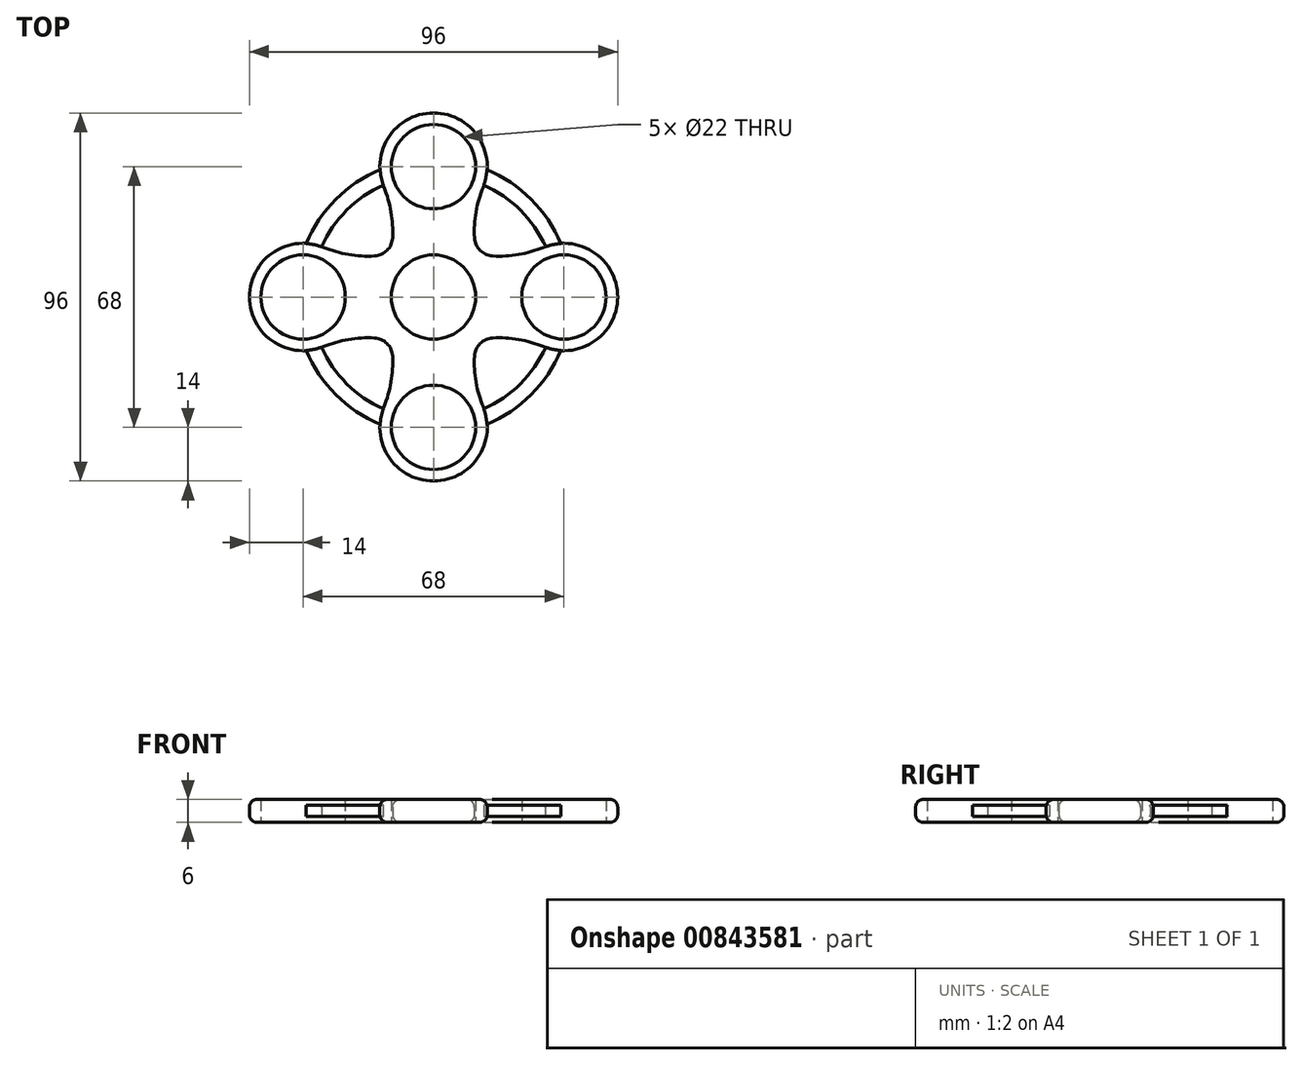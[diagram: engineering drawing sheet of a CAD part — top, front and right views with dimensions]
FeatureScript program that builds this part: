
annotation { "Feature Type Name" : "Feature", "Feature Type Description" : "" }
export const myFeature = defineFeature(function(context is Context, id is Id, definition is map)
    precondition{}
    {
        {
            var Q0;
            Q0=qCreatedBy(makeId("Top.planeOp"),FACE);
            var sketch = newSketch(context, id + "F0", { "sketchPlane" : qUnion([Q0])});
            skCircle(sketch, "E0", {"center": v(0, 0) * mm, "radius": 11 * mm});
            skLineSegment(sketch, "E1", {"start": v(0, 0) * mm, "end": v(0, 14) * mm});
            skCircle(sketch, "E2", {"center": v(0, 34) * mm, "radius": 11 * mm});
            skArc(sketch, "E3", {"start": v(12.94, 28.66) * mm, "mid": v(0, 48) * mm, "end": v(-12.94, 28.66) * mm});
            skArc(sketch, "E4", {"start": v(12.94, 28.66) * mm, "mid": v(11.07, 22.16) * mm, "end": v(10.68, 15.4) * mm});
            skArc(sketch, "E5.MirrorCS", {"start": v(-12.94, 28.66) * mm, "mid": v(-11.07, 22.16) * mm, "end": v(-10.68, 15.4) * mm});
            skArc(sketch, "E6.1.0", {"start": v(-28.66, 12.94) * mm, "mid": v(-22.16, 11.07) * mm, "end": v(-15.4, 10.68) * mm});
            skArc(sketch, "E6.1.1", {"start": v(-28.66, 12.94) * mm, "mid": v(-48, 0) * mm, "end": v(-28.66, -12.94) * mm});
            skCircle(sketch, "E6.1.2", {"center": v(-34, 0) * mm, "radius": 11 * mm});
            skArc(sketch, "E6.1.3", {"start": v(-28.66, -12.94) * mm, "mid": v(-22.16, -11.07) * mm, "end": v(-15.4, -10.68) * mm});
            skArc(sketch, "E6.2.0", {"start": v(-12.94, -28.66) * mm, "mid": v(-11.07, -22.16) * mm, "end": v(-10.68, -15.4) * mm});
            skArc(sketch, "E6.2.1", {"start": v(-12.94, -28.66) * mm, "mid": v(0, -48) * mm, "end": v(12.94, -28.66) * mm});
            skCircle(sketch, "E6.2.2", {"center": v(0, -34) * mm, "radius": 11 * mm});
            skArc(sketch, "E6.2.3", {"start": v(12.94, -28.66) * mm, "mid": v(11.07, -22.16) * mm, "end": v(10.68, -15.4) * mm});
            skArc(sketch, "E6.3.0", {"start": v(28.66, -12.94) * mm, "mid": v(22.16, -11.07) * mm, "end": v(15.4, -10.68) * mm});
            skArc(sketch, "E6.3.1", {"start": v(28.66, -12.94) * mm, "mid": v(48, 0) * mm, "end": v(28.66, 12.94) * mm});
            skCircle(sketch, "E6.3.2", {"center": v(34, 0) * mm, "radius": 11 * mm});
            skArc(sketch, "E6.3.3", {"start": v(28.66, 12.94) * mm, "mid": v(22.16, 11.07) * mm, "end": v(15.4, 10.68) * mm});
            skPoint(sketch, "E7.visualSharp", {"position": v(-11.2, 11.2) * mm});
            skArc(sketch, "E7.filletArc", {"start": v(-15.4, 10.68) * mm, "mid": v(-12.13, 12.13) * mm, "end": v(-10.68, 15.4) * mm});
            skPoint(sketch, "E8.visualSharp", {"position": v(11.2, 11.2) * mm});
            skArc(sketch, "E8.filletArc", {"start": v(10.68, 15.4) * mm, "mid": v(12.13, 12.13) * mm, "end": v(15.4, 10.68) * mm});
            skPoint(sketch, "E9.visualSharp", {"position": v(-11.2, -11.2) * mm});
            skArc(sketch, "E9.filletArc", {"start": v(-10.68, -15.4) * mm, "mid": v(-12.13, -12.13) * mm, "end": v(-15.4, -10.68) * mm});
            skPoint(sketch, "E10.visualSharp", {"position": v(11.2, -11.2) * mm});
            skArc(sketch, "E10.filletArc", {"start": v(15.4, -10.68) * mm, "mid": v(12.13, -12.13) * mm, "end": v(10.68, -15.4) * mm});
            skSolve(sketch);
        }
        {
            var Q0;
            Q0 = qSketchRegion(id + "F0", true);
            extrude(context, id + "F1", {"entities" : qUnion([Q0]), "oppositeDirection" : true, "depth" : 1.5 * mm, "offsetDistance" : 25 * mm});
        }
        {
            var Q0;
            Q0=qCreatedBy(makeId("Top.planeOp"),FACE);
            var sketch = newSketch(context, id + "F2", { "sketchPlane" : qUnion([Q0])});
            skCircle(sketch, "E11", {"center": v(0, 0) * mm, "radius": 11 * mm});
            skCircle(sketch, "E12", {"center": v(0, 34) * mm, "radius": 11 * mm});
            skCircle(sketch, "E13.1.0", {"center": v(-34, 0) * mm, "radius": 11 * mm});
            skCircle(sketch, "E13.2.0", {"center": v(0, -34) * mm, "radius": 11 * mm});
            skCircle(sketch, "E13.3.0", {"center": v(34, 0) * mm, "radius": 11 * mm});
            skArc(sketch, "E14", {"start": v(12.94, 28.66) * mm, "mid": v(13.05, 28.92) * mm, "end": v(13.14, 29.18) * mm});
            skPoint(sketch, "E15.start.orphan", {"position": v(0, 17) * mm});
            skArc(sketch, "E16", {"start": v(12.94, 28.66) * mm, "mid": v(11.07, 22.16) * mm, "end": v(10.68, 15.4) * mm});
            skArc(sketch, "E17.MirrorC", {"start": v(-12.94, 28.66) * mm, "mid": v(-11.07, 22.16) * mm, "end": v(-10.68, 15.4) * mm});
            skArc(sketch, "E18.1.0", {"start": v(-28.66, 12.94) * mm, "mid": v(-22.16, 11.07) * mm, "end": v(-15.4, 10.68) * mm});
            skArc(sketch, "E18.1.1", {"start": v(-28.66, -12.94) * mm, "mid": v(-22.16, -11.07) * mm, "end": v(-15.4, -10.68) * mm});
            skArc(sketch, "E18.2.1", {"start": v(12.94, -28.66) * mm, "mid": v(11.07, -22.16) * mm, "end": v(10.68, -15.4) * mm});
            skArc(sketch, "E18.3.0", {"start": v(28.66, -12.94) * mm, "mid": v(22.16, -11.07) * mm, "end": v(15.4, -10.68) * mm});
            skArc(sketch, "E18.3.1", {"start": v(28.66, 12.94) * mm, "mid": v(22.16, 11.07) * mm, "end": v(15.4, 10.68) * mm});
            skArc(sketch, "E19", {"start": v(-28.66, 12.94) * mm, "mid": v(-28.92, 13.05) * mm, "end": v(-29.18, 13.14) * mm});
            skArc(sketch, "E20", {"start": v(-12.94, -28.66) * mm, "mid": v(-13.05, -28.92) * mm, "end": v(-13.14, -29.18) * mm});
            skArc(sketch, "E21", {"start": v(28.66, -12.94) * mm, "mid": v(28.92, -13.05) * mm, "end": v(29.18, -13.14) * mm});
            skArc(sketch, "E22.trimOffspring", {"start": v(-12.94, -28.66) * mm, "mid": v(-11.07, -22.16) * mm, "end": v(-10.68, -15.4) * mm});
            skPoint(sketch, "E23.visualSharp", {"position": v(-11.2, 11.2) * mm});
            skArc(sketch, "E23.filletArc", {"start": v(-15.4, 10.68) * mm, "mid": v(-12.13, 12.13) * mm, "end": v(-10.68, 15.4) * mm});
            skPoint(sketch, "E24.visualSharp", {"position": v(-11.2, -11.2) * mm});
            skArc(sketch, "E24.filletArc", {"start": v(-10.68, -15.4) * mm, "mid": v(-12.13, -12.13) * mm, "end": v(-15.4, -10.68) * mm});
            skPoint(sketch, "E25.visualSharp", {"position": v(11.2, 11.2) * mm});
            skArc(sketch, "E25.filletArc", {"start": v(10.68, 15.4) * mm, "mid": v(12.13, 12.13) * mm, "end": v(15.4, 10.68) * mm});
            skPoint(sketch, "E26.visualSharp", {"position": v(11.2, -11.2) * mm});
            skArc(sketch, "E26.filletArc", {"start": v(15.4, -10.68) * mm, "mid": v(12.13, -12.13) * mm, "end": v(10.68, -15.4) * mm});
            skArc(sketch, "E27", {"start": v(-13.98, 33.18) * mm, "mid": v(-25.46, 25.46) * mm, "end": v(-33.18, 13.98) * mm});
            skArc(sketch, "E28", {"start": v(-13.14, 29.18) * mm, "mid": v(-22.63, 22.63) * mm, "end": v(-29.18, 13.14) * mm});
            skArc(sketch, "E29.trimOffspring", {"start": v(-13.14, 29.18) * mm, "mid": v(-13.05, 28.92) * mm, "end": v(-12.94, 28.66) * mm});
            skArc(sketch, "E30.trimOffspring", {"start": v(-33.18, 13.98) * mm, "mid": v(-48, 0) * mm, "end": v(-33.18, -13.98) * mm});
            skArc(sketch, "E31.trimOffspring", {"start": v(-29.18, -13.14) * mm, "mid": v(-22.63, -22.63) * mm, "end": v(-13.14, -29.18) * mm});
            skArc(sketch, "E32.trimOffspring", {"start": v(-33.18, -13.98) * mm, "mid": v(-25.46, -25.46) * mm, "end": v(-13.98, -33.18) * mm});
            skArc(sketch, "E33.trimOffspring", {"start": v(-29.18, -13.14) * mm, "mid": v(-28.92, -13.05) * mm, "end": v(-28.66, -12.94) * mm});
            skArc(sketch, "E34.trimOffspring", {"start": v(-13.98, -33.18) * mm, "mid": v(0, -48) * mm, "end": v(13.98, -33.18) * mm});
            skArc(sketch, "E35.trimOffspring", {"start": v(13.14, -29.18) * mm, "mid": v(22.63, -22.63) * mm, "end": v(29.18, -13.14) * mm});
            skArc(sketch, "E36.trimOffspring", {"start": v(13.98, -33.18) * mm, "mid": v(25.46, -25.46) * mm, "end": v(33.18, -13.98) * mm});
            skArc(sketch, "E37.trimOffspring", {"start": v(13.14, -29.18) * mm, "mid": v(13.05, -28.92) * mm, "end": v(12.94, -28.66) * mm});
            skArc(sketch, "E38.trimOffspring", {"start": v(29.18, 13.14) * mm, "mid": v(22.63, 22.63) * mm, "end": v(13.14, 29.18) * mm});
            skArc(sketch, "E39.trimOffspring", {"start": v(33.18, 13.98) * mm, "mid": v(25.46, 25.46) * mm, "end": v(13.98, 33.18) * mm});
            skArc(sketch, "E40.trimOffspring", {"start": v(33.18, -13.98) * mm, "mid": v(48, 0) * mm, "end": v(33.18, 13.98) * mm});
            skArc(sketch, "E41.trimOffspring", {"start": v(29.18, 13.14) * mm, "mid": v(28.92, 13.05) * mm, "end": v(28.66, 12.94) * mm});
            skArc(sketch, "E42.trimOffspring", {"start": v(13.98, 33.18) * mm, "mid": v(0, 48) * mm, "end": v(-13.98, 33.18) * mm});
            skSolve(sketch);
        }
        {
            var Q0;
            Q0 = qSketchRegion(id + "F2", true);
            extrude(context, id + "F3", {"entities" : qUnion([Q0]), "depth" : 3 * mm, "offsetDistance" : 25 * mm});
        }
        {
            var Q0;
            Q0=qCreatedBy(makeId("Top.planeOp"),FACE);
            cPlane(context, id + "F4", {"entities" : qUnion([Q0]), "cplaneType" : CPlaneType.OFFSET, "offset" : 1.5 * mm, "width" : 150 * mm, "height" : 150 * mm});
        }
        {
            var Q0;
            Q0=makeQuery(id+"F1.opExtrude","SWEPT_BODY",BODY,{"disambiguationData":[OSD([sQuery(id+"F0.wireOp",EDGE,"E0"),sQuery(id+"F0.wireOp",EDGE,"E2"),sQuery(id+"F0.wireOp",EDGE,"E3"),sQuery(id+"F0.wireOp",EDGE,"E4"),sQuery(id+"F0.wireOp",EDGE,"E5.MirrorCS"),sQuery(id+"F0.wireOp",EDGE,"E6.1.0"),sQuery(id+"F0.wireOp",EDGE,"E6.1.1"),sQuery(id+"F0.wireOp",EDGE,"E6.1.2"),sQuery(id+"F0.wireOp",EDGE,"E6.1.3"),sQuery(id+"F0.wireOp",EDGE,"E6.2.0"),sQuery(id+"F0.wireOp",EDGE,"E6.2.1"),sQuery(id+"F0.wireOp",EDGE,"E6.2.2"),sQuery(id+"F0.wireOp",EDGE,"E6.2.3"),sQuery(id+"F0.wireOp",EDGE,"E6.3.0"),sQuery(id+"F0.wireOp",EDGE,"E6.3.1"),sQuery(id+"F0.wireOp",EDGE,"E6.3.2"),sQuery(id+"F0.wireOp",EDGE,"E6.3.3"),sQuery(id+"F0.wireOp",EDGE,"E7.filletArc"),sQuery(id+"F0.wireOp",EDGE,"E8.filletArc"),sQuery(id+"F0.wireOp",EDGE,"E9.filletArc"),sQuery(id+"F0.wireOp",EDGE,"E10.filletArc")])]});
            var Q1;
            Q1=qCreatedBy(id+"F4.planeOp",FACE);
            mirror(context, id + "F5", {"operationType" : NewBodyOperationType.ADD, "entities" : qUnion([Q0]), "mirrorPlane" : qUnion([Q1])});
        }
        {
            var Q0;
            Q0=makeQuery(id+"F5.opPattern","COPY",EDGE,{"derivedFrom":makeQuery(id+"F1.opExtrude","CAP_EDGE",EDGE,{"disambiguationData":[OSD([sQuery(id+"F0.wireOp",EDGE,"E6.2.1")])],"isStart":false}),"instanceName":"1"});
            var Q1;
            Q1=makeQuery(id+"F1.opExtrude","CAP_EDGE",EDGE,{"disambiguationData":[OSD([sQuery(id+"F0.wireOp",EDGE,"E6.2.1")])],"isStart":false});
            fillet(context, id + "F6", {"entities" : qUnion([Q0, Q1]), "radius" : 2 * mm, "tangentPropagation" : true, "allowEdgeOverflow" : false});
        }
    });
